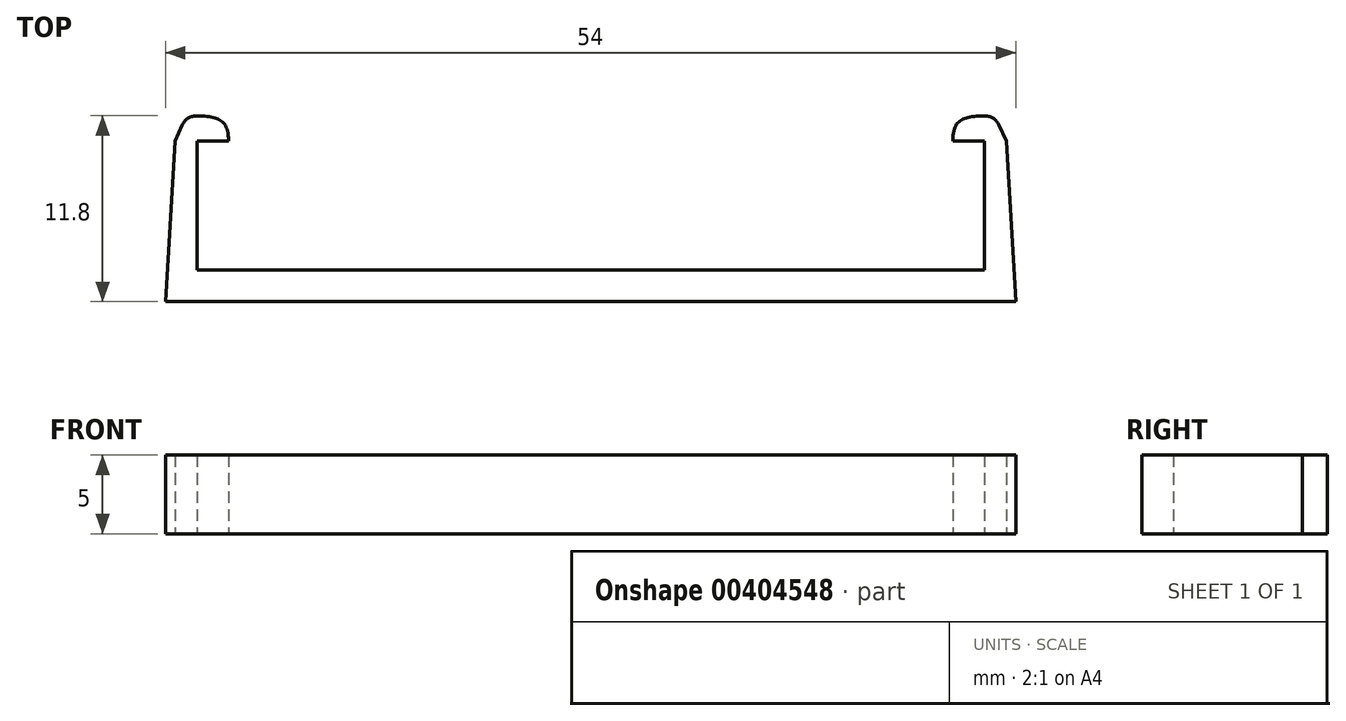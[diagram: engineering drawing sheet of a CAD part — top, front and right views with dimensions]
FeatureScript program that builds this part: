
annotation { "Feature Type Name" : "Feature", "Feature Type Description" : "" }
export const myFeature = defineFeature(function(context is Context, id is Id, definition is map)
    precondition{}
    {
        {
            var Q0;
            Q0=qCreatedBy(makeId("Top.planeOp"),FACE);
            var sketch = newSketch(context, id + "F0", { "sketchPlane" : qUnion([Q0])});
            skLineSegment(sketch, "E0", {"start": v(0, 10.62) * mm, "end": v(0, -5.42) * mm, "construction": true});
            skLineSegment(sketch, "E1.bottom", {"start": v(0, 0) * mm, "end": v(-25, 0) * mm});
            skLineSegment(sketch, "E1.top", {"start": v(0, 2) * mm, "end": v(-25, 2) * mm});
            skLineSegment(sketch, "E1.left", {"start": v(0, 0) * mm, "end": v(0, 2) * mm});
            skLineSegment(sketch, "E1.right", {"start": v(-25, 0) * mm, "end": v(-25, 2) * mm});
            skLineSegment(sketch, "E2.bottom", {"start": v(-25, 0) * mm, "end": v(-27, 0) * mm});
            skLineSegment(sketch, "E2.top", {"start": v(-25, 10.2) * mm, "end": v(-26.4, 10.2) * mm});
            skLineSegment(sketch, "E2.left", {"start": v(-25, 0) * mm, "end": v(-25, 10.2) * mm});
            skLineSegment(sketch, "E2.right", {"start": v(-27, 0) * mm, "end": v(-26.4, 10.2) * mm});
            skLineSegment(sketch, "E3.bottom", {"start": v(-26.4, 10.2) * mm, "end": v(-23, 10.2) * mm});
            skLineSegment(sketch, "E3.left", {"start": v(-26.4, 10.2) * mm, "end": v(-25.66, 11.82) * mm});
            skFitSpline(sketch, "E4", {"points": [v(-23, 10.2) * mm, v(-25.66, 11.82) * mm], "startDerivative": vector(-0.05, 4.89) * mm, "endDerivative": vector(-5.3, 0.17) * mm});
            skLineSegment(sketch, "E5.MirrorCS", {"start": v(25, 10.2) * mm, "end": v(26.4, 10.2) * mm});
            skLineSegment(sketch, "E6.MirrorCS", {"start": v(25, 0) * mm, "end": v(25, 2) * mm});
            skLineSegment(sketch, "E7.MirrorCS", {"start": v(25, 0) * mm, "end": v(25, 10.2) * mm});
            skLineSegment(sketch, "E8.MirrorCS", {"start": v(27, 0) * mm, "end": v(26.4, 10.2) * mm});
            skFitSpline(sketch, "E9.MirrorCS", {"points": [v(23, 10.2) * mm, v(25.66, 11.82) * mm], "startDerivative": vector(0.05, 4.89) * mm, "endDerivative": vector(5.3, 0.17) * mm});
            skLineSegment(sketch, "E10.MirrorCS", {"start": v(25, 0) * mm, "end": v(27, 0) * mm});
            skLineSegment(sketch, "E11.MirrorCS", {"start": v(26.4, 10.2) * mm, "end": v(25.66, 11.82) * mm});
            skLineSegment(sketch, "E12.MirrorCS", {"start": v(26.4, 10.2) * mm, "end": v(23, 10.2) * mm});
            skLineSegment(sketch, "E13.MirrorCS", {"start": v(0, 2) * mm, "end": v(25, 2) * mm});
            skLineSegment(sketch, "E14.MirrorCS", {"start": v(0, 0) * mm, "end": v(25, 0) * mm});
            skSolve(sketch);
        }
        {
            var Q0;
            {var subQ2=sQuery(id+"F0.wireOp",EDGE,"E3.left");Q0=makeQuery(id+"F0.imprint","IMPRINT",FACE,{"disambiguationData":[TD([[makeQuery(id+"F0.imprint","IMPRINT",EDGE,{"derivedFrom":subQ2}),-1.0]])]});}
            var Q1;
            {var subQ5=sQuery(id+"F0.wireOp",EDGE,"E2.bottom");Q1=makeQuery(id+"F0.imprint","IMPRINT",FACE,{"disambiguationData":[TD([[makeQuery(id+"F0.imprint","IMPRINT",EDGE,{"derivedFrom":subQ5}),-1.0]])]});}
            var Q2;
            {var subQ0=sQuery(id+"F0.wireOp",EDGE,"E1.bottom");Q2=makeQuery(id+"F0.imprint","IMPRINT",FACE,{"disambiguationData":[TD([[makeQuery(id+"F0.imprint","IMPRINT",EDGE,{"derivedFrom":subQ0}),-1.0]])]});}
            var Q3;
            Q3=makeQuery(id+"F0.imprint","IMPRINT",FACE,{"disambiguationData":[TD([[makeQuery(id+"F0.imprint","IMPRINT",EDGE,{"derivedFrom":sQuery(id+"F0.wireOp",EDGE,"E1.left")}),-1.0]])]});
            var Q4;
            {var subQ1=sQuery(id+"F0.wireOp",EDGE,"E8.MirrorCS");Q4=makeQuery(id+"F0.imprint","IMPRINT",FACE,{"disambiguationData":[TD([[makeQuery(id+"F0.imprint","IMPRINT",EDGE,{"derivedFrom":subQ1}),1.0]])]});}
            var Q5;
            {var subQ0=sQuery(id+"F0.wireOp",EDGE,"E9.MirrorCS");Q5=makeQuery(id+"F0.imprint","IMPRINT",FACE,{"disambiguationData":[TD([[makeQuery(id+"F0.imprint","IMPRINT",EDGE,{"derivedFrom":subQ0}),-1.0]])]});}
            extrude(context, id + "F1", {"entities" : qUnion([Q0, Q1, Q2, Q3, Q4, Q5]), "depth" : 5 * mm});
        }
        {
            var Q0;
            Q0=makeQuery(id+"F1.opExtrude","SWEPT_EDGE",EDGE,{"disambiguationData":[OSD([sQuery(id+"F0.wireOp",EDGE,"E9.MirrorCS"),sQuery(id+"F0.wireOp",EDGE,"E11.MirrorCS")])]});
            fillet(context, id + "F2", {"entities" : qUnion([Q0]), "radius" : 1 * mm, "tangentPropagation" : true, "allowEdgeOverflow" : false});
        }
        {
            var Q0;
            Q0=makeQuery(id+"F1.opExtrude","SWEPT_EDGE",EDGE,{"disambiguationData":[OSD([sQuery(id+"F0.wireOp",EDGE,"E3.left"),sQuery(id+"F0.wireOp",EDGE,"E4")])]});
            fillet(context, id + "F3", {"entities" : qUnion([Q0]), "radius" : 1 * mm, "tangentPropagation" : true, "allowEdgeOverflow" : false});
        }
    });
